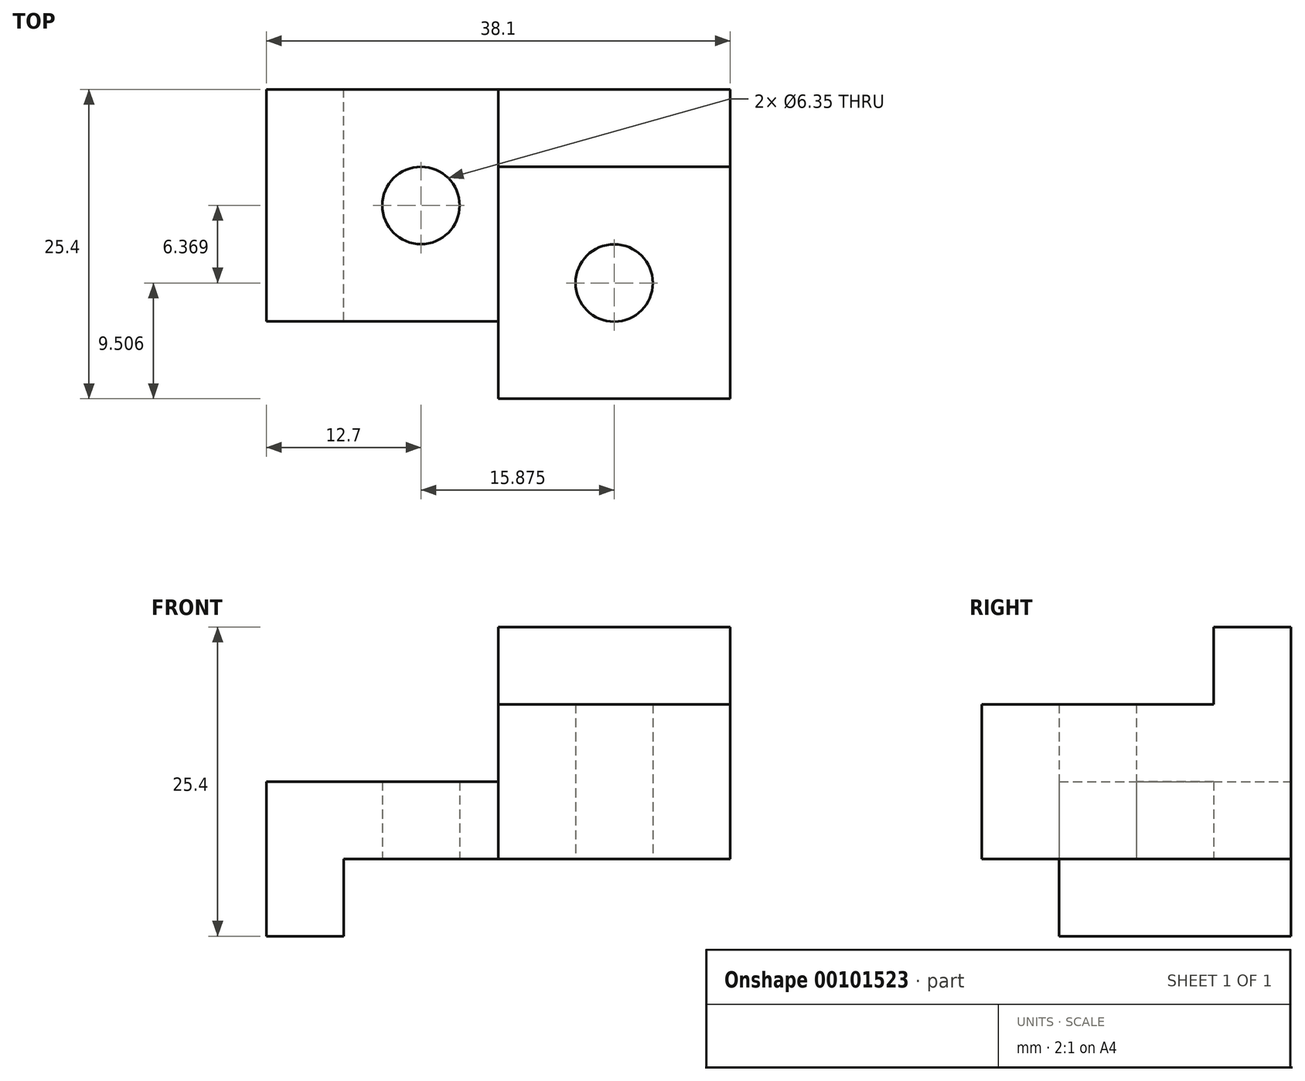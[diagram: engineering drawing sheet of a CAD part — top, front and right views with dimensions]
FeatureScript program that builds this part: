
annotation { "Feature Type Name" : "Feature", "Feature Type Description" : "" }
export const myFeature = defineFeature(function(context is Context, id is Id, definition is map)
    precondition{}
    {
        {
            var Q0;
            Q0=qCreatedBy(makeId("Top.planeOp"),FACE);
            var sketch = newSketch(context, id + "F0", { "sketchPlane" : qUnion([Q0])});
            skLineSegment(sketch, "E0.bottom", {"start": v(0, 0) * mm, "end": v(38.1, 0) * mm});
            skLineSegment(sketch, "E0.top", {"start": v(0, -25.4) * mm, "end": v(38.1, -25.4) * mm});
            skLineSegment(sketch, "E0.left", {"start": v(0, 0) * mm, "end": v(0, -25.4) * mm});
            skLineSegment(sketch, "E0.right", {"start": v(38.1, 0) * mm, "end": v(38.1, -25.4) * mm});
            skSolve(sketch);
        }
        {
            var Q0;
            Q0 = qSketchRegion(id + "F0", true);
            extrude(context, id + "F1", {"entities" : qUnion([Q0]), "depth" : 25.4 * mm});
        }
        {
            var Q0;
            Q0=qCreatedBy(makeId("Top.planeOp"),FACE);
            var sketch = newSketch(context, id + "F2", { "sketchPlane" : qUnion([Q0])});
            skLineSegment(sketch, "E1.bottom", {"start": v(0, 0) * mm, "end": v(19.05, 0) * mm});
            skLineSegment(sketch, "E1.top", {"start": v(0, -19.05) * mm, "end": v(19.05, -19.05) * mm});
            skLineSegment(sketch, "E1.left", {"start": v(0, 0) * mm, "end": v(0, -19.05) * mm});
            skLineSegment(sketch, "E1.right", {"start": v(19.05, 0) * mm, "end": v(19.05, -19.05) * mm});
            skLineSegment(sketch, "E2.top", {"start": v(0, -25.4) * mm, "end": v(19.05, -25.4) * mm});
            skLineSegment(sketch, "E2.left", {"start": v(0, -19.05) * mm, "end": v(0, -25.4) * mm});
            skLineSegment(sketch, "E2.right", {"start": v(19.05, -19.05) * mm, "end": v(19.05, -25.4) * mm});
            skSolve(sketch);
        }
        {
            var Q0;
            Q0=makeQuery(id+"F2.imprint","IMPRINT",FACE,{"disambiguationData":[TD([[makeQuery(id+"F2.imprint","IMPRINT",EDGE,{"derivedFrom":sQuery(id+"F2.wireOp",EDGE,"E1.top")}),-1.0]])]});
            extrude(context, id + "F3", {"entities" : qUnion([Q0]), "operationType" : NewBodyOperationType.REMOVE, "endBound" : BoundingType.THROUGH_ALL, "depth" : 25.4 * mm});
        }
        {
            var Q0;
            Q0=qCreatedBy(makeId("Front.planeOp"),FACE);
            var sketch = newSketch(context, id + "F4", { "sketchPlane" : qUnion([Q0])});
            skLineSegment(sketch, "E3.bottom", {"start": v(0, 0) * mm, "end": v(6.35, 0) * mm});
            skLineSegment(sketch, "E3.top", {"start": v(0, 6.35) * mm, "end": v(6.35, 6.35) * mm});
            skLineSegment(sketch, "E3.left", {"start": v(0, 0) * mm, "end": v(0, 6.35) * mm});
            skLineSegment(sketch, "E3.right", {"start": v(6.35, 0) * mm, "end": v(6.35, 6.35) * mm});
            skLineSegment(sketch, "E4.bottom", {"start": v(6.35, 6.35) * mm, "end": v(38.1, 6.35) * mm});
            skLineSegment(sketch, "E4.top", {"start": v(6.35, 0) * mm, "end": v(38.1, 0) * mm});
            skLineSegment(sketch, "E4.left", {"start": v(6.35, 6.35) * mm, "end": v(6.35, 0) * mm});
            skLineSegment(sketch, "E4.right", {"start": v(38.1, 6.35) * mm, "end": v(38.1, 0) * mm});
            skLineSegment(sketch, "E5.bottom", {"start": v(0, 6.35) * mm, "end": v(6.58, 6.35) * mm});
            skLineSegment(sketch, "E5.top", {"start": v(0, 12.7) * mm, "end": v(6.58, 12.7) * mm});
            skLineSegment(sketch, "E5.left", {"start": v(0, 6.35) * mm, "end": v(0, 12.7) * mm});
            skLineSegment(sketch, "E5.right", {"start": v(6.58, 6.35) * mm, "end": v(6.58, 12.7) * mm});
            skLineSegment(sketch, "E6.bottom", {"start": v(0, 12.7) * mm, "end": v(19.05, 12.7) * mm});
            skLineSegment(sketch, "E6.top", {"start": v(0, 25.4) * mm, "end": v(19.05, 25.4) * mm});
            skLineSegment(sketch, "E6.left", {"start": v(0, 12.7) * mm, "end": v(0, 25.4) * mm});
            skLineSegment(sketch, "E6.right", {"start": v(19.05, 12.7) * mm, "end": v(19.05, 25.4) * mm});
            skSolve(sketch);
        }
        {
            var Q0;
            Q0=makeQuery(id+"F4.imprint","IMPRINT",FACE,{"disambiguationData":[TD([[makeQuery(id+"F4.imprint","IMPRINT",EDGE,{"derivedFrom":sQuery(id+"F4.wireOp",EDGE,"E6.top")}),-1.0]])]});
            var Q1;
            {var subQ1=sQuery(id+"F4.wireOp",EDGE,"E4.bottom");Q1=makeQuery(id+"F4.imprint","IMPRINT",FACE,{"disambiguationData":[TD([[makeQuery(id+"F4.imprint","IMPRINT",EDGE,{"derivedFrom":subQ1}),-1.0]])]});}
            extrude(context, id + "F5", {"entities" : qUnion([Q0, Q1]), "operationType" : NewBodyOperationType.REMOVE, "endBound" : BoundingType.THROUGH_ALL, "depth" : 25.4 * mm});
        }
        {
            var Q0;
            Q0=qCreatedBy(makeId("Right.planeOp"),FACE);
            var sketch = newSketch(context, id + "F6", { "sketchPlane" : qUnion([Q0])});
            skLineSegment(sketch, "E7.bottom", {"start": v(0, 0) * mm, "end": v(-6.35, 0) * mm});
            skLineSegment(sketch, "E7.top", {"start": v(0, 25.4) * mm, "end": v(-6.35, 25.4) * mm});
            skLineSegment(sketch, "E7.left", {"start": v(0, 0) * mm, "end": v(0, 25.4) * mm});
            skLineSegment(sketch, "E7.right", {"start": v(-6.35, 0) * mm, "end": v(-6.35, 25.4) * mm});
            skLineSegment(sketch, "E8.bottom", {"start": v(-6.35, 25.4) * mm, "end": v(-25.4, 25.4) * mm});
            skLineSegment(sketch, "E8.top", {"start": v(-6.35, 19.05) * mm, "end": v(-25.4, 19.05) * mm});
            skLineSegment(sketch, "E8.left", {"start": v(-6.35, 25.4) * mm, "end": v(-6.35, 19.05) * mm});
            skLineSegment(sketch, "E8.right", {"start": v(-25.4, 25.4) * mm, "end": v(-25.4, 19.05) * mm});
            skSolve(sketch);
        }
        {
            var Q0;
            Q0=makeQuery(id+"F6.imprint","IMPRINT",FACE,{"disambiguationData":[TD([[makeQuery(id+"F6.imprint","IMPRINT",EDGE,{"derivedFrom":sQuery(id+"F6.wireOp",EDGE,"E8.bottom")}),1.0]])]});
            extrude(context, id + "F7", {"entities" : qUnion([Q0]), "operationType" : NewBodyOperationType.REMOVE, "endBound" : BoundingType.THROUGH_ALL, "depth" : 25.4 * mm});
        }
        {
            var Q0;
            Q0=qCreatedBy(makeId("Top.planeOp"),FACE);
            var sketch = newSketch(context, id + "F8", { "sketchPlane" : qUnion([Q0])});
            skLineSegment(sketch, "E9.bottom", {"start": v(0, 0) * mm, "end": v(19.05, 0) * mm});
            skLineSegment(sketch, "E9.top", {"start": v(0, -12.7) * mm, "end": v(19.05, -12.7) * mm});
            skLineSegment(sketch, "E9.left", {"start": v(0, 0) * mm, "end": v(0, -12.7) * mm});
            skLineSegment(sketch, "E9.right", {"start": v(19.05, 0) * mm, "end": v(19.05, -12.7) * mm});
            skLineSegment(sketch, "E10.bottom", {"start": v(19.05, -12.7) * mm, "end": v(38.1, -12.7) * mm});
            skLineSegment(sketch, "E10.top", {"start": v(19.05, -19.05) * mm, "end": v(38.1, -19.05) * mm});
            skLineSegment(sketch, "E10.left", {"start": v(19.05, -12.7) * mm, "end": v(19.05, -19.05) * mm});
            skLineSegment(sketch, "E10.right", {"start": v(38.1, -12.7) * mm, "end": v(38.1, -19.05) * mm});
            skCircle(sketch, "E11", {"center": v(28.58, -15.9) * mm, "radius": 3.18 * mm});
            skSolve(sketch);
        }
        {
            var Q0;
            {var subQ0=sQuery(id+"F8.wireOp",EDGE,"E11");var subQ1=sQuery(id+"F8.wireOp",EDGE,"E10.top");var subQ2=makeQuery(id+"F8.imprint","INTERSECT",VERTEX,{"disambiguationData":[OD(0.0)],"derivedFrom":[subQ1,subQ0]});Q0=makeQuery(id+"F8.imprint","IMPRINT",FACE,{"disambiguationData":[TD([[makeQuery(id+"F8.imprint","IMPRINT",EDGE,{"disambiguationData":[TD([[subQ2,-1.0]])],"derivedFrom":subQ1}),-1.0]])]});}
            var Q1;
            {var subQ0=sQuery(id+"F8.wireOp",EDGE,"E11");var subQ1=sQuery(id+"F8.wireOp",EDGE,"E10.top");var subQ2=makeQuery(id+"F8.imprint","INTERSECT",VERTEX,{"disambiguationData":[OD(0.0)],"derivedFrom":[subQ1,subQ0]});Q1=makeQuery(id+"F8.imprint","IMPRINT",FACE,{"disambiguationData":[TD([[makeQuery(id+"F8.imprint","IMPRINT",EDGE,{"disambiguationData":[TD([[subQ2,-1.0]])],"derivedFrom":subQ1}),1.0]])]});}
            extrude(context, id + "F9", {"entities" : qUnion([Q0, Q1]), "operationType" : NewBodyOperationType.REMOVE, "endBound" : BoundingType.THROUGH_ALL, "depth" : 25.4 * mm});
        }
        {
            var Q0;
            Q0=qCreatedBy(makeId("Top.planeOp"),FACE);
            var sketch = newSketch(context, id + "F10", { "sketchPlane" : qUnion([Q0])});
            skLineSegment(sketch, "E12.bottom", {"start": v(0, 0) * mm, "end": v(12.7, 0) * mm});
            skLineSegment(sketch, "E12.top", {"start": v(0, -9.53) * mm, "end": v(12.7, -9.53) * mm});
            skLineSegment(sketch, "E12.left", {"start": v(0, 0) * mm, "end": v(0, -9.53) * mm});
            skLineSegment(sketch, "E12.right", {"start": v(12.7, 0) * mm, "end": v(12.7, -9.53) * mm});
            skCircle(sketch, "E13", {"center": v(12.7, -9.53) * mm, "radius": 3.18 * mm});
            skSolve(sketch);
        }
        {
            var Q0;
            {var subQ0=sQuery(id+"F10.wireOp",EDGE,"E12.right");var subQ1=sQuery(id+"F10.wireOp",EDGE,"E12.top");var subQ2=makeQuery(id+"F10.imprint","INTERSECT",VERTEX,{"derivedFrom":[subQ1,subQ0]});Q0=makeQuery(id+"F10.imprint","IMPRINT",FACE,{"disambiguationData":[TD([[makeQuery(id+"F10.imprint","IMPRINT",EDGE,{"disambiguationData":[TD([[subQ2,1.0]])],"derivedFrom":subQ1}),-1.0]])]});}
            var Q1;
            {var subQ0=sQuery(id+"F10.wireOp",EDGE,"E12.right");var subQ1=sQuery(id+"F10.wireOp",EDGE,"E12.top");var subQ2=makeQuery(id+"F10.imprint","INTERSECT",VERTEX,{"derivedFrom":[subQ1,subQ0]});Q1=makeQuery(id+"F10.imprint","IMPRINT",FACE,{"disambiguationData":[TD([[makeQuery(id+"F10.imprint","IMPRINT",EDGE,{"disambiguationData":[TD([[subQ2,1.0]])],"derivedFrom":subQ1}),1.0]])]});}
            extrude(context, id + "F11", {"entities" : qUnion([Q0, Q1]), "operationType" : NewBodyOperationType.REMOVE, "endBound" : BoundingType.THROUGH_ALL, "depth" : 25.4 * mm});
        }
    });
